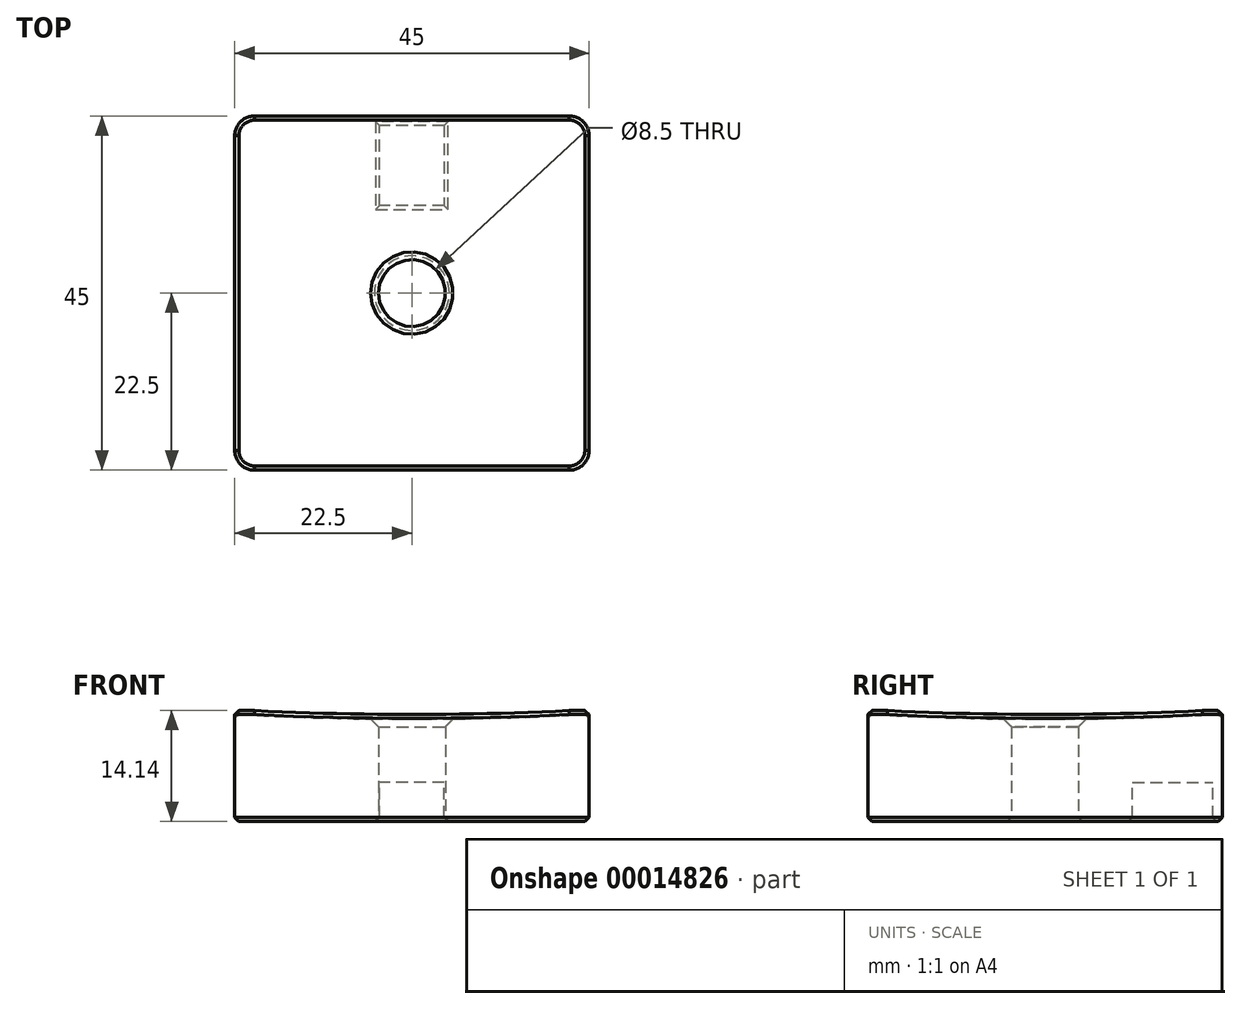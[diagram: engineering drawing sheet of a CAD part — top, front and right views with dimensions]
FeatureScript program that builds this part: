
annotation { "Feature Type Name" : "Feature", "Feature Type Description" : "" }
export const myFeature = defineFeature(function(context is Context, id is Id, definition is map)
    precondition{}
    {
        {
            var Q0;
            Q0=qCreatedBy(makeId("Top.planeOp"),FACE);
            var sketch = newSketch(context, id + "F0", { "sketchPlane" : qUnion([Q0])});
            skLineSegment(sketch, "E0.bottom", {"start": v(-22.5, -22.5) * mm, "end": v(22.5, -22.5) * mm});
            skLineSegment(sketch, "E0.top", {"start": v(-22.5, 22.5) * mm, "end": v(22.5, 22.5) * mm});
            skLineSegment(sketch, "E0.left", {"start": v(-22.5, -22.5) * mm, "end": v(-22.5, 22.5) * mm});
            skLineSegment(sketch, "E0.right", {"start": v(22.5, -22.5) * mm, "end": v(22.5, 22.5) * mm});
            skLineSegment(sketch, "E1", {"start": v(0, 0) * mm, "end": v(0, 22.5) * mm, "construction": true});
            skLineSegment(sketch, "E2", {"start": v(0, 0) * mm, "end": v(-22.5, 0) * mm, "construction": true});
            skSolve(sketch);
        }
        {
            var Q0;
            Q0 = qSketchRegion(id + "F0", true);
            extrude(context, id + "F1", {"entities" : qUnion([Q0]), "depth" : 23 * mm});
        }
        {
            var Q0;
            Q0=qCreatedBy(makeId("Front.planeOp"),FACE);
            var sketch = newSketch(context, id + "F2", { "sketchPlane" : qUnion([Q0])});
            skArc(sketch, "E3", {"start": v(-400, 395) * mm, "mid": v(0, 13) * mm, "end": v(400, 395) * mm, "construction": true});
            skLineSegment(sketch, "E4", {"start": v(0, 413.42) * mm, "end": v(0, 0) * mm, "construction": true});
            skLineSegment(sketch, "E5", {"start": v(-400, 395) * mm, "end": v(400, 395) * mm, "construction": true});
            skLineSegment(sketch, "E6", {"start": v(0, 13) * mm, "end": v(22.5, 13) * mm, "construction": true});
            skSolve(sketch);
        }
        {
            var Q0;
            Q0=makeQuery(id+"F1.opExtrude","CAP_FACE",FACE,{"disambiguationData":[OSD([sQuery(id+"F0.wireOp",EDGE,"E0.bottom"),sQuery(id+"F0.wireOp",EDGE,"E0.top"),sQuery(id+"F0.wireOp",EDGE,"E0.left"),sQuery(id+"F0.wireOp",EDGE,"E0.right")])],"isStart":false});
            cPlane(context, id + "F3", {"entities" : qUnion([Q0]), "cplaneType" : CPlaneType.OFFSET, "offset" : 372 * mm, "width" : 150 * mm, "height" : 150 * mm});
        }
        {
            var Q0;
            Q0=qCreatedBy(id+"F3.planeOp",FACE);
            var sketch = newSketch(context, id + "F4", { "sketchPlane" : qUnion([Q0])});
            skArc(sketch, "E7", {"start": v(-370.8, 150) * mm, "mid": v(-400, 0) * mm, "end": v(-370.8, -150) * mm});
            skLineSegment(sketch, "E8", {"start": v(-370.8, 150) * mm, "end": v(-370.8, -150) * mm});
            skSolve(sketch);
        }
        {
            var Q0;
            Q0 = qSketchRegion(id + "F4", true);
            var Q1;
            Q1=sQuery(id+"F2.wireOp",EDGE,"E3");
            revolve(context, id + "F5", {"operationType" : NewBodyOperationType.REMOVE, "entities" : qUnion([Q0]), "axis" : qUnion([Q1]), "revolveType" : RevolveType.FULL, "oppositeDirection" : true});
        }
        {
            var Q0;
            Q0=makeQuery(id+"F1.opExtrude","CAP_FACE",FACE,{"disambiguationData":[OSD([sQuery(id+"F0.wireOp",EDGE,"E0.bottom"),sQuery(id+"F0.wireOp",EDGE,"E0.top"),sQuery(id+"F0.wireOp",EDGE,"E0.left"),sQuery(id+"F0.wireOp",EDGE,"E0.right")])],"isStart":true});
            var sketch = newSketch(context, id + "F6", { "sketchPlane" : qUnion([Q0])});
            skCircle(sketch, "E9", {"center": v(0, 0) * mm, "radius": 4.25 * mm});
            skSolve(sketch);
        }
        {
            var Q0;
            Q0 = qSketchRegion(id + "F6", true);
            extrude(context, id + "F7", {"entities" : qUnion([Q0]), "operationType" : NewBodyOperationType.REMOVE, "endBound" : BoundingType.THROUGH_ALL, "oppositeDirection" : true, "depth" : 25 * mm});
        }
        {
            var Q0;
            Q0=makeQuery(id+"F1.opExtrude","SWEPT_EDGE",EDGE,{"disambiguationData":[OSD([sQuery(id+"F0.wireOp",EDGE,"E0.bottom"),sQuery(id+"F0.wireOp",EDGE,"E0.left")])]});
            var Q1;
            Q1=makeQuery(id+"F1.opExtrude","SWEPT_EDGE",EDGE,{"disambiguationData":[OSD([sQuery(id+"F0.wireOp",EDGE,"E0.bottom"),sQuery(id+"F0.wireOp",EDGE,"E0.right")])]});
            var Q2;
            Q2=makeQuery(id+"F1.opExtrude","SWEPT_EDGE",EDGE,{"disambiguationData":[OSD([sQuery(id+"F0.wireOp",EDGE,"E0.top"),sQuery(id+"F0.wireOp",EDGE,"E0.right")])]});
            var Q3;
            Q3=makeQuery(id+"F1.opExtrude","SWEPT_EDGE",EDGE,{"disambiguationData":[OSD([sQuery(id+"F0.wireOp",EDGE,"E0.top"),sQuery(id+"F0.wireOp",EDGE,"E0.left")])]});
            fillet(context, id + "F8", {"entities" : qUnion([Q0, Q1, Q2, Q3]), "radius" : 2.5 * mm, "tangentPropagation" : true, "allowEdgeOverflow" : false});
        }
        {
            var Q0;
            Q0=makeQuery(id+"F1.opExtrude","SWEPT_FACE",FACE,{"disambiguationData":[OSD([sQuery(id+"F0.wireOp",EDGE,"E0.top")])]});
            var sketch = newSketch(context, id + "F9", { "sketchPlane" : qUnion([Q0])});
            skLineSegment(sketch, "E10.bottom", {"start": v(-4.1, 0) * mm, "end": v(4.1, 0) * mm});
            skLineSegment(sketch, "E10.top", {"start": v(-4.1, 5) * mm, "end": v(4.1, 5) * mm});
            skLineSegment(sketch, "E10.left", {"start": v(-4.1, 0) * mm, "end": v(-4.1, 5) * mm});
            skLineSegment(sketch, "E10.right", {"start": v(4.1, 0) * mm, "end": v(4.1, 5) * mm});
            skLineSegment(sketch, "E11", {"start": v(0, 0) * mm, "end": v(0, 5) * mm, "construction": true});
            skSolve(sketch);
        }
        {
            var Q0;
            Q0 = qSketchRegion(id + "F9", true);
            extrude(context, id + "F10", {"entities" : qUnion([Q0]), "operationType" : NewBodyOperationType.REMOVE, "oppositeDirection" : true, "depth" : 11.4 * mm});
        }
        {
            var Q0;
            Q0=makeQuery(id+"F9.imprint","IMPRINT",FACE,{"disambiguationData":[TD([[makeQuery(id+"F9.imprint","IMPRINT",EDGE,{"derivedFrom":sQuery(id+"F9.wireOp",EDGE,"E10.bottom")}),-1.0]])]});
            extrude(context, id + "F11", {"entities" : qUnion([Q0]), "operationType" : NewBodyOperationType.ADD, "oppositeDirection" : true, "depth" : 1.2 * mm});
        }
        {
            var Q0;
            Q0=makeQuery(id+"F11.boolean.opBoolean","MERGE",FACE,{"derivedFrom":[makeQuery(id+"F1.opExtrude","CAP_FACE",FACE,{"disambiguationData":[OSD([sQuery(id+"F0.wireOp",EDGE,"E0.bottom"),sQuery(id+"F0.wireOp",EDGE,"E0.top"),sQuery(id+"F0.wireOp",EDGE,"E0.left"),sQuery(id+"F0.wireOp",EDGE,"E0.right")])],"isStart":true}),makeQuery(id+"F11.opExtrude","SWEPT_FACE",FACE,{"disambiguationData":[OSD([sQuery(id+"F9.wireOp",EDGE,"E10.bottom")])]})]});
            chamfer(context, id + "F12", {"entities" : qUnion([Q0]), "width" : .5 * mm, "tangentPropagation" : true});
        }
        {
            var Q0;
            Q0=makeQuery(id+"F7.boolean.opBoolean","INTERSECT",EDGE,{"derivedFrom":[makeQuery(id+"F5.boolean.opBoolean","COPY",FACE,{"derivedFrom":makeQuery(id+"F5.opRevolve","SWEPT_FACE",FACE,{"disambiguationData":[OSD([sQuery(id+"F4.wireOp",EDGE,"E7")])]})}),makeQuery(id+"F7.opExtrude","SWEPT_FACE",FACE,{"disambiguationData":[OSD([sQuery(id+"F6.wireOp",EDGE,"E9")])]})]});
            chamfer(context, id + "F13", {"entities" : qUnion([Q0]), "width" : 1 * mm, "tangentPropagation" : true});
        }
        {
            var Q0;
            Q0=makeQuery(id+"F5.boolean.opBoolean","INTERSECT",EDGE,{"derivedFrom":[makeQuery(id+"F1.opExtrude","SWEPT_FACE",FACE,{"disambiguationData":[OSD([sQuery(id+"F0.wireOp",EDGE,"E0.top")])]}),makeQuery(id+"F5.opRevolve","SWEPT_FACE",FACE,{"disambiguationData":[OSD([sQuery(id+"F4.wireOp",EDGE,"E7")])]})]});
            chamfer(context, id + "F14", {"entities" : qUnion([Q0]), "width" : .5 * mm, "tangentPropagation" : true});
        }
    });
